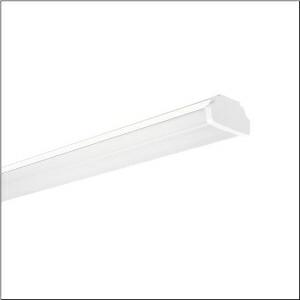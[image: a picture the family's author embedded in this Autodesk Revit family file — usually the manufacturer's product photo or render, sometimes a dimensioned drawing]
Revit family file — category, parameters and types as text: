
# Revit family: modario_31_gen_2_53bm812cv685c2_9c12
name_source: partatom
category: Lighting Fixtures
units: mm (PartAtom-declared; Revit-internal decimal feet)

## family parameters
Cut with Voids When Loaded = No
Host = Face
Light Source = No
Part Type = Normal
Room Calculation Point = No
Round Connector Dimension = Use Diameter
Shared = No

## types (1)
- --- (1 x LED, 8970 lm, 49.9 W, 6500K)
    Apparent Load = 50 VA
    CIE Flux Codes = 47 80 95 93 100
    Color Rendering = 80
    Color Temperature = 6500K
    Default Elevation = 1800 mm
    Description = Modario 31 Gen.2, luminaire insert, of sheet steel, coil coated, white, length: 1.495mm, width: 81mm, height: 82mm, 5x system unit, system units: 299mm, LED rated luminous flux: 8.970lm, light colour: 865, SDCM (Standard Deviation of Colour Matching)MacAdam ≤ 3 SDCM (initial), control gear: ON/OFF Multilumen, CLOi, with plug, 3-pole, with phase selection, mains connection: 220..240V, AC, 50/60Hz, start of lifetime: 50W, end of service life: 61W, through-wiring accessed according to module size, primary optical cover: cover, of PMMA, light emission: direct distribution, primary light characteristic: symmetric, protection rating (complete): IP20, protection rating (LED compartment): IP50, insulation class (complete): insulation class I (protective earthing), certification: CE, ENEC, VDE, UKCA, impact resistance: IK03, permissible ambient temperature for indoor applications: -35..+40°C, corresponds to IFS (International Featured Standards) requirements for safety and quality in the food industry, reducing of maximum allowable ambient temperature of 5°C with ceiling mounting, IP40 when using the optional accessory 5TP9018, packaging unit: 1 piece
    Height = 92 mm
    Lamp = 1 x LED
    Lamp Light Flux = 8970 lm
    Lamp Power = 49.9 W
    Lamp count = 1
    Length = 1495 mm
    Luminous efficacy = 180 lm/W
    Manufacturer = Siteco
    ModVariant = No
    Model = 53BM812CV685C2
    Mounting Place = Ceiling
    Mounting Type = Pendant
    Number of Poles = 1
    OnlyDefault = Yes
    Power Factor = 1
    Product Name = Modario 31 Gen.2
    Product group = luminaire insert | ceiling pendant
    ProductGroupID = 901
    Protection Class = Protection class I
    Protection Degree = IP 20
    RLX_Detail_Level = 1
    RLX_Emergency_Light_Flux = 0 lm
    RLX_Emergency_Type = 0
    RLX_Emergency_Type_DB = No
    RlxData = <blob elided: 40497 chars, md5=3356ee5a>
    Socket = socket
    Standby Power = 0 W
    System Light Flux = 8970 lm
    System Power = 50 W
    Type Comments = factory setting: luminous flux: 100 % | (A | C | E) | 116 mA
    Type Image = l_1341886.jpg
    URL = http://relux.com
    VarID = @adj_050769
    Voltage = 0 V
    Weight = 0.00 kg
    Width = 81 mm

## geometry (parser evidence)
native form markers: Blend x4, Sweep x11
no freeform markers — native parametric forms only
